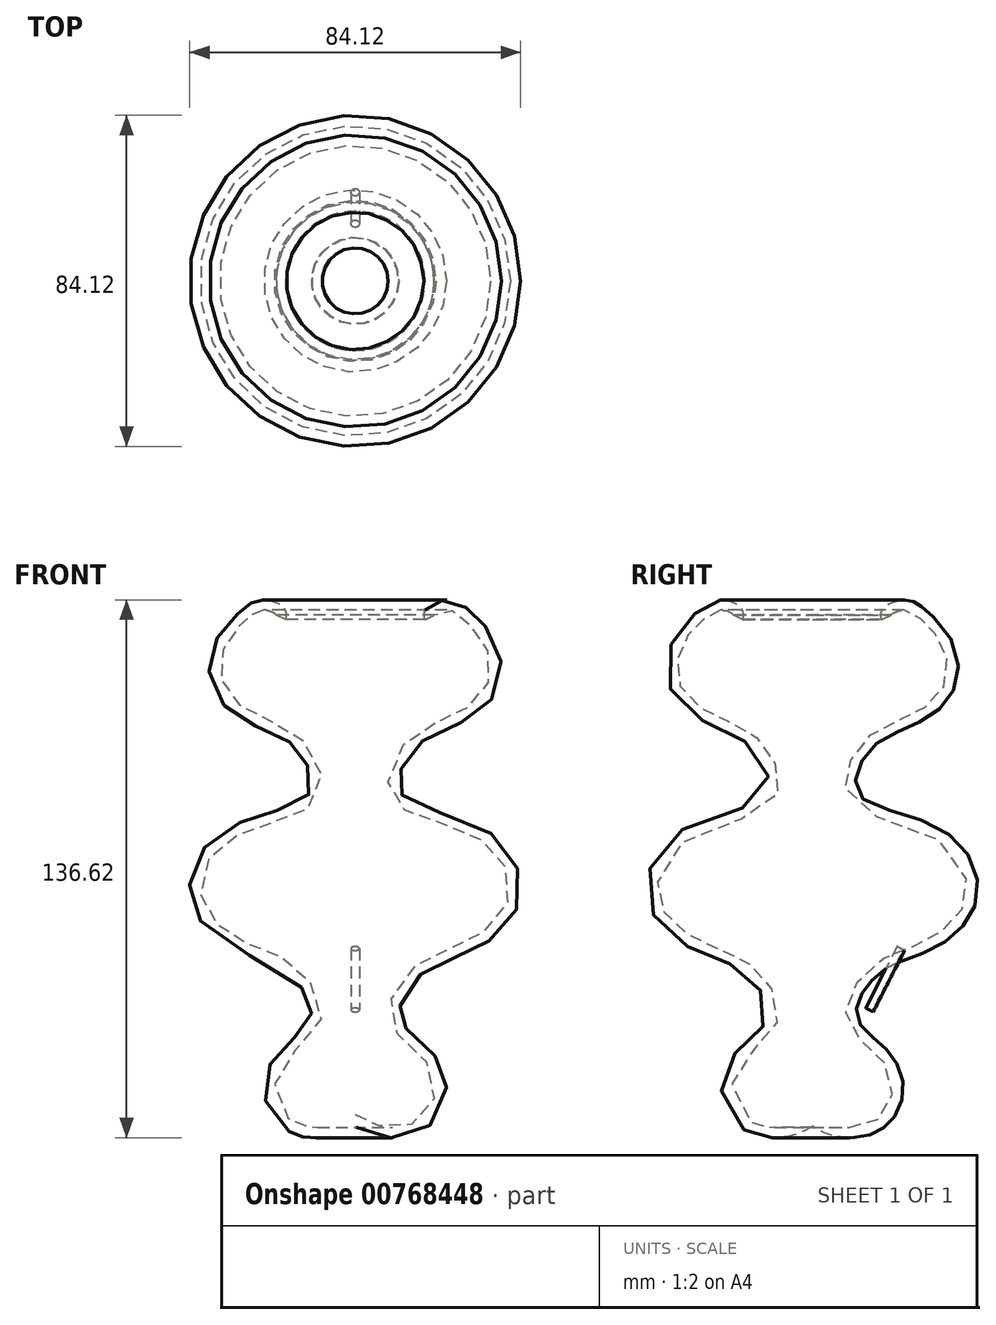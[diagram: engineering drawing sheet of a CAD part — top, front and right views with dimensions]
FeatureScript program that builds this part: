
annotation { "Feature Type Name" : "Feature", "Feature Type Description" : "" }
export const myFeature = defineFeature(function(context is Context, id is Id, definition is map)
    precondition{}
    {
        {
            var Q0;
            Q0=qCreatedBy(makeId("Front.planeOp"),FACE);
            var sketch = newSketch(context, id + "F0", { "sketchPlane" : qUnion([Q0])});
            skLineSegment(sketch, "E0", {"start": v(0, 74.79) * mm, "end": v(0, -74.79) * mm});
            skFitSpline(sketch, "E1", {"points": [v(0, -66.31) * mm, v(6.27, -69.25) * mm, v(17.45, -66.93) * mm, v(19.34, -54.77) * mm, v(8.8, -42.6) * mm, v(15.28, -28.54) * mm, v(28, -22.58) * mm, v(38.81, -12.58) * mm, v(36.1, 0) * mm, v(22.31, 7.44) * mm, v(9.06, 14.47) * mm, v(12.85, 28.26) * mm, v(25.83, 35.57) * mm, v(33.67, 42.87) * mm, v(33.13, 52.88) * mm, v(27.72, 59.37) * mm, v(23.16, 61.78) * mm, v(20.06, 60.5) * mm], "startDerivative": vector(120.55, -69.86) * mm, "endDerivative": vector(15.57, -32.13) * mm});
            skFitSpline(sketch, "E2.0", {"points": [v(-1.3, -68.56) * mm, v(-0.73, -68.9) * mm, v(0.2, -69.48) * mm, v(1.69, -70.3) * mm, v(2.94, -70.91) * mm, v(4.11, -71.36) * mm, v(5.13, -71.66) * mm, v(6.21, -71.91) * mm, v(7.64, -72.13) * mm, v(9.45, -72.23) * mm, v(11.31, -72.14) * mm, v(13.2, -71.85) * mm, v(15.1, -71.32) * mm, v(16.93, -70.52) * mm, v(18.37, -69.59) * mm, v(19.43, -68.66) * mm, v(20.39, -67.63) * mm, v(21.39, -66.2) * mm, v(22.28, -64.31) * mm, v(22.87, -62.3) * mm, v(23.14, -60.2) * mm, v(23.08, -58.06) * mm, v(22.73, -56.28) * mm, v(22.26, -54.88) * mm, v(21.89, -54.03) * mm, v(21.53, -53.37) * mm, v(21.15, -52.72) * mm, v(20.63, -51.97) * mm, v(19.96, -51.12) * mm, v(19.01, -50.06) * mm, v(17.77, -48.85) * mm, v(16.26, -47.52) * mm, v(14.82, -46.27) * mm, v(13.52, -45.07) * mm, v(12.64, -44.13) * mm, v(12.08, -43.4) * mm, v(11.74, -42.89) * mm, v(11.48, -42.4) * mm, v(11.33, -42) * mm, v(11.24, -41.7) * mm, v(11.17, -41.38) * mm, v(11.11, -40.95) * mm, v(11.1, -40.39) * mm, v(11.16, -39.57) * mm, v(11.4, -38.45) * mm, v(11.94, -37) * mm, v(12.7, -35.5) * mm, v(13.64, -34.05) * mm, v(14.73, -32.67) * mm, v(15.7, -31.63) * mm, v(16.52, -30.89) * mm, v(17.12, -30.39) * mm, v(17.73, -29.93) * mm, v(18.56, -29.37) * mm, v(19.62, -28.76) * mm, v(21.4, -27.9) * mm, v(23.34, -27.17) * mm, v(25.43, -26.42) * mm, v(27.07, -25.8) * mm, v(28.49, -25.22) * mm, v(29.65, -24.69) * mm, v(30.8, -24.1) * mm, v(32.25, -23.31) * mm, v(33.95, -22.23) * mm, v(35.57, -21.02) * mm, v(37.1, -19.68) * mm, v(38.5, -18.2) * mm, v(39.73, -16.58) * mm, v(40.58, -15.1) * mm, v(41.13, -13.84) * mm, v(41.58, -12.53) * mm, v(41.93, -10.86) * mm, v(42.06, -8.83) * mm, v(41.9, -6.81) * mm, v(41.5, -4.84) * mm, v(40.87, -2.93) * mm, v(40.02, -1.11) * mm, v(38.97, 0.6) * mm, v(37.72, 2.17) * mm, v(36.31, 3.56) * mm, v(34.27, 5.19) * mm, v(31.46, 6.83) * mm, v(27.83, 8.38) * mm, v(24.66, 9.44) * mm, v(22.07, 10.23) * mm, v(19.53, 10.99) * mm, v(17.12, 11.76) * mm, v(15.05, 12.62) * mm, v(13.72, 13.3) * mm, v(12.66, 14.03) * mm, v(12.03, 14.65) * mm, v(11.66, 15.14) * mm, v(11.47, 15.45) * mm, v(11.36, 15.7) * mm, v(11.25, 15.98) * mm, v(11.13, 16.37) * mm, v(11.04, 16.89) * mm, v(10.97, 17.66) * mm, v(11.02, 18.75) * mm, v(11.29, 20.2) * mm, v(11.76, 21.7) * mm, v(12.43, 23.2) * mm, v(13.26, 24.63) * mm, v(14.06, 25.71) * mm, v(14.74, 26.49) * mm, v(15.44, 27.2) * mm, v(16.4, 28.01) * mm, v(17.67, 28.88) * mm, v(19.05, 29.66) * mm, v(21, 30.62) * mm, v(23.08, 31.5) * mm, v(25.23, 32.41) * mm, v(26.57, 33.03) * mm, v(27.64, 33.57) * mm, v(28.69, 34.13) * mm, v(29.95, 34.9) * mm, v(31.39, 35.91) * mm, v(32.72, 37.05) * mm, v(33.93, 38.3) * mm, v(35, 39.72) * mm, v(35.72, 41.01) * mm, v(36.19, 42.13) * mm, v(36.57, 43.27) * mm, v(36.89, 44.72) * mm, v(37.1, 47.09) * mm, v(36.92, 49.45) * mm, v(36.38, 51.72) * mm, v(35.9, 53.09) * mm, v(35.42, 54.14) * mm, v(34.9, 55.14) * mm, v(34.17, 56.3) * mm, v(33.22, 57.54) * mm, v(32.23, 58.66) * mm, v(31.4, 59.5) * mm, v(30.74, 60.13) * mm, v(30.26, 60.57) * mm, v(29.88, 60.93) * mm, v(29.58, 61.2) * mm, v(29.29, 61.46) * mm, v(28.91, 61.8) * mm, v(28.29, 62.35) * mm, v(27.6, 62.9) * mm, v(26.8, 63.4) * mm, v(26.15, 63.76) * mm, v(25.43, 64.06) * mm, v(24.64, 64.28) * mm, v(23.93, 64.37) * mm, v(23.35, 64.4) * mm, v(22.9, 64.38) * mm, v(22.48, 64.34) * mm, v(21.94, 64.25) * mm, v(21.29, 64.1) * mm, v(20.69, 63.92) * mm, v(20.23, 63.75) * mm, v(19.9, 63.6) * mm, v(19.59, 63.46) * mm, v(19.28, 63.3) * mm, v(18.97, 63.11) * mm, v(18.66, 62.89) * mm, v(18.36, 62.64) * mm, v(18.1, 62.35) * mm, v(17.88, 62.06) * mm, v(17.65, 61.64) * mm, v(17.5, 61.14) * mm, v(17.44, 60.64) * mm, v(17.46, 60.08) * mm, v(17.59, 59.63) * mm, v(17.72, 59.37) * mm]});
            skFitSpline(sketch, "E3", {"points": [v(0, -66.31) * mm, v(0, -69.34) * mm], "startDerivative": vector(0, -3.03) * mm, "endDerivative": vector(0, -3.03) * mm});
            skFitSpline(sketch, "E4", {"points": [v(20.06, 60.5) * mm, v(17.72, 59.37) * mm], "startDerivative": vector(-2.34, -1.13) * mm, "endDerivative": vector(-2.34, -1.13) * mm});
            skSolve(sketch);
        }
        {
            var Q0;
            Q0=makeQuery(id+"F0.imprint","IMPRINT",FACE,{"disambiguationData":[TD([[makeQuery(id+"F0.imprint","IMPRINT",EDGE,{"derivedFrom":sQuery(id+"F0.wireOp",EDGE,"E1")}),-1.0]])]});
            var Q1;
            Q1=sQuery(id+"F0.wireOp",EDGE,"E0");
            revolve(context, id + "F1", {"surfaceOperationType" : NewSurfaceOperationType.NEW, "entities" : qUnion([Q0]), "axis" : qUnion([Q1]), "revolveType" : RevolveType.FULL});
        }
        {
            var Q0;
            Q0=qCreatedBy(makeId("Right.planeOp"),FACE);
            var sketch = newSketch(context, id + "F2", { "sketchPlane" : qUnion([Q0])});
            skLineSegment(sketch, "E5", {"start": v(-34.8, 5.14) * mm, "end": v(-42.8, -10.47) * mm});
            skSolve(sketch);
        }
        {
            var Q0;
            Q0=sQuery(id+"F2.wireOp",VERTEX,"E5.start");
            var Q1;
            Q1=sQuery(id+"F2.wireOp",EDGE,"E5");
            cPlane(context, id + "F3", {"entities" : qUnion([Q0, Q1]), "cplaneType" : CPlaneType.CURVE_POINT, "offset" : 25 * mm, "width" : 150 * mm, "height" : 150 * mm});
        }
        {
            var Q0;
            Q0=qCreatedBy(id+"F3.planeOp",FACE);
            var sketch = newSketch(context, id + "F4", { "sketchPlane" : qUnion([Q0])});
            skCircle(sketch, "E6", {"center": v(0, -31.04) * mm, "radius": 1.06 * mm});
            skSolve(sketch);
        }
        {
            var Q0;
            Q0=makeQuery(id+"F4.imprint","IMPRINT",FACE,{"disambiguationData":[TD([[makeQuery(id+"F4.imprint","IMPRINT",EDGE,{"derivedFrom":sQuery(id+"F4.wireOp",EDGE,"E6")}),1.0]])]});
            var Q1;
            Q1=sQuery(id+"F2.wireOp",EDGE,"E5");
            sweep(context, id + "F5", {"profiles" : qUnion([Q0]), "path" : qUnion([Q1])});
        }
    });
